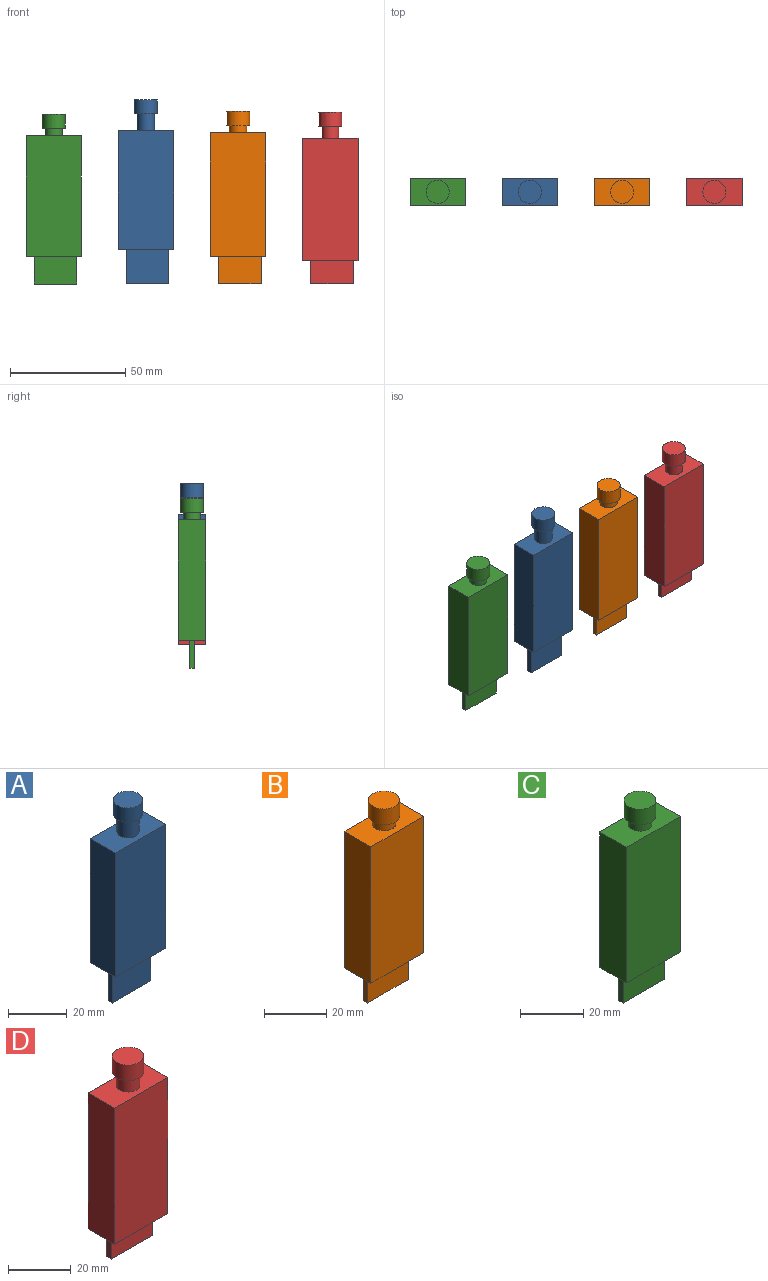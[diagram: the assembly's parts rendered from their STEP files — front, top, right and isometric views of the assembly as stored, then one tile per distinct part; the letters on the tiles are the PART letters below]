
ASSEMBLY  parts=4 mates=4
PART A: 15 faces, bbox 24x12x79.8 mm
  f0: cylinder r=3.75mm len=7.5mm, axis (0,0,1), area 172mm2, adj f5,f13
  f1: plane 51.5x24mm, normal (0,1,0), area 1236mm2, adj f2,f4,f5,f10
  f2: plane 51.5x12mm, normal (-1,0,0), area 618mm2, adj f1,f3,f5,f10
  f3: plane 51.5x24mm, normal (0,-1,0), area 1236mm2, adj f2,f4,f5,f10
  f4: plane 51.5x12mm, normal (1,0,0), area 618mm2, adj f1,f3,f5,f10
  f5: plane 24x12mm, normal (0,0,1), area 243.8mm2, adj f0,f1,f2,f3,f4
  f6: plane 15x2mm, normal (-1,0,0), area 30mm2, adj f7,f9,f10,f11
  f7: plane 18.5x15mm, normal (0,-1,0), area 277.5mm2, adj f6,f8,f10,f11
  f8: plane 15x2mm, normal (1,0,0), area 30mm2, adj f7,f9,f10,f11
  f9: plane 18.5x15mm, normal (0,1,0), area 277.5mm2, adj f6,f8,f10,f11
  f10: plane 24x12mm, normal (0,0,-1), area 251mm2, adj f1,f2,f3,f4,f6,f7,f8,f9
  f11: plane 18.5x2mm, normal (0,0,-1), area 37mm2, adj f6,f7,f8,f9
  f12: cylinder r=5mm len=10mm, axis (0,0,1), area 188.5mm2, adj f13,f14
  f13: plane 10x10mm, normal (0,0,-1), area 34.4mm2, adj f0,f12
  f14: plane 10x10mm, normal (0,0,1), area 78.5mm2, adj f12
PART B: 15 faces, bbox 24x12x74.9 mm
  f0: cylinder r=3.75mm len=7.5mm, axis (0,0,1), area 75.4mm2, adj f5,f13
  f1: plane 53.5x24mm, normal (0,1,0), area 1284mm2, adj f2,f4,f5,f10
  f2: plane 53.5x12mm, normal (-1,0,0), area 642mm2, adj f1,f3,f5,f10
  f3: plane 53.5x24mm, normal (0,-1,0), area 1284mm2, adj f2,f4,f5,f10
  f4: plane 53.5x12mm, normal (1,0,0), area 642mm2, adj f1,f3,f5,f10
  f5: plane 24x12mm, normal (0,0,1), area 243.8mm2, adj f0,f1,f2,f3,f4
  f6: plane 12x2mm, normal (-1,0,0), area 24mm2, adj f7,f9,f10,f11
  f7: plane 18.5x12mm, normal (0,-1,0), area 222mm2, adj f6,f8,f10,f11
  f8: plane 12x2mm, normal (1,0,0), area 24mm2, adj f7,f9,f10,f11
  f9: plane 18.5x12mm, normal (0,1,0), area 222mm2, adj f6,f8,f10,f11
  f10: plane 24x12mm, normal (0,0,-1), area 251mm2, adj f1,f2,f3,f4,f6,f7,f8,f9
  f11: plane 18.5x2mm, normal (0,0,-1), area 37mm2, adj f6,f7,f8,f9
  f12: cylinder r=5mm len=10mm, axis (0,0,1), area 194.8mm2, adj f13,f14
  f13: plane 10x10mm, normal (0,0,-1), area 34.4mm2, adj f0,f12
  f14: plane 10x10mm, normal (0,0,1), area 78.5mm2, adj f12
PART C: 15 faces, bbox 24x12x73.6 mm
  f0: cylinder r=3.75mm len=7.5mm, axis (0,0,1), area 77.8mm2, adj f5,f13
  f1: plane 52.3x24mm, normal (0,1,0), area 1255.2mm2, adj f2,f4,f5,f10
  f2: plane 52.3x12mm, normal (-1,0,0), area 627.6mm2, adj f1,f3,f5,f10
  f3: plane 52.3x24mm, normal (0,-1,0), area 1255.2mm2, adj f2,f4,f5,f10
  f4: plane 52.3x12mm, normal (1,0,0), area 627.6mm2, adj f1,f3,f5,f10
  f5: plane 24x12mm, normal (0,0,1), area 243.8mm2, adj f0,f1,f2,f3,f4
  f6: plane 12x2mm, normal (-1,0,0), area 24mm2, adj f7,f9,f10,f11
  f7: plane 18.5x12mm, normal (0,-1,0), area 222mm2, adj f6,f8,f10,f11
  f8: plane 12x2mm, normal (1,0,0), area 24mm2, adj f7,f9,f10,f11
  f9: plane 18.5x12mm, normal (0,1,0), area 222mm2, adj f6,f8,f10,f11
  f10: plane 24x12mm, normal (0,0,-1), area 251mm2, adj f1,f2,f3,f4,f6,f7,f8,f9
  f11: plane 18.5x2mm, normal (0,0,-1), area 37mm2, adj f6,f7,f8,f9
  f12: cylinder r=5mm len=10mm, axis (0,0,1), area 188.5mm2, adj f13,f14
  f13: plane 10x10mm, normal (0,0,-1), area 34.4mm2, adj f0,f12
  f14: plane 10x10mm, normal (0,0,1), area 78.5mm2, adj f12
PART D: 15 faces, bbox 24x12x74.5 mm
  f0: cylinder r=3.75mm len=7.5mm, axis (0,0,1), area 124.9mm2, adj f5,f13
  f1: plane 53.1x24mm, normal (0,1,0), area 1274.4mm2, adj f2,f4,f5,f10
  f2: plane 53.1x12mm, normal (-1,0,0), area 637.2mm2, adj f1,f3,f5,f10
  f3: plane 53.1x24mm, normal (0,-1,0), area 1274.4mm2, adj f2,f4,f5,f10
  f4: plane 53.1x12mm, normal (1,0,0), area 637.2mm2, adj f1,f3,f5,f10
  f5: plane 24x12mm, normal (0,0,1), area 243.8mm2, adj f0,f1,f2,f3,f4
  f6: plane 10x2mm, normal (-1,0,0), area 20mm2, adj f7,f9,f10,f11
  f7: plane 18.5x10mm, normal (0,-1,0), area 185mm2, adj f6,f8,f10,f11
  f8: plane 10x2mm, normal (1,0,0), area 20mm2, adj f7,f9,f10,f11
  f9: plane 18.5x10mm, normal (0,1,0), area 185mm2, adj f6,f8,f10,f11
  f10: plane 24x12mm, normal (0,0,-1), area 251mm2, adj f1,f2,f3,f4,f6,f7,f8,f9
  f11: plane 18.5x2mm, normal (0,0,-1), area 37mm2, adj f6,f7,f8,f9
  f12: cylinder r=5mm len=10mm, axis (0,0,1), area 191.6mm2, adj f13,f14
  f13: plane 10x10mm, normal (0,0,-1), area 34.4mm2, adj f0,f12
  f14: plane 10x10mm, normal (0,0,1), area 78.5mm2, adj f12
PLACE A t=(-46.14,0,-4.08)mm
PLACE B t=(-6.14,0,-4.08)mm
PLACE C t=(-86.14,0,-4.13)mm
PLACE D t=(33.86,0,-4.08)mm
MATE parallel A.f11 <-> C.f11  axis (0,0,-1) through (-45.39,0,-4.08)mm
MATE parallel D.f2 <-> B.f4  axis (-1,0,0) through (21.86,-6,5.92)mm
MATE parallel B.f2 <-> A.f4  axis (-1,0,0) through (-18.14,-6,7.92)mm
MATE parallel A.f2 <-> C.f4  axis (-1,0,0) through (-58.14,0,36.67)mm
